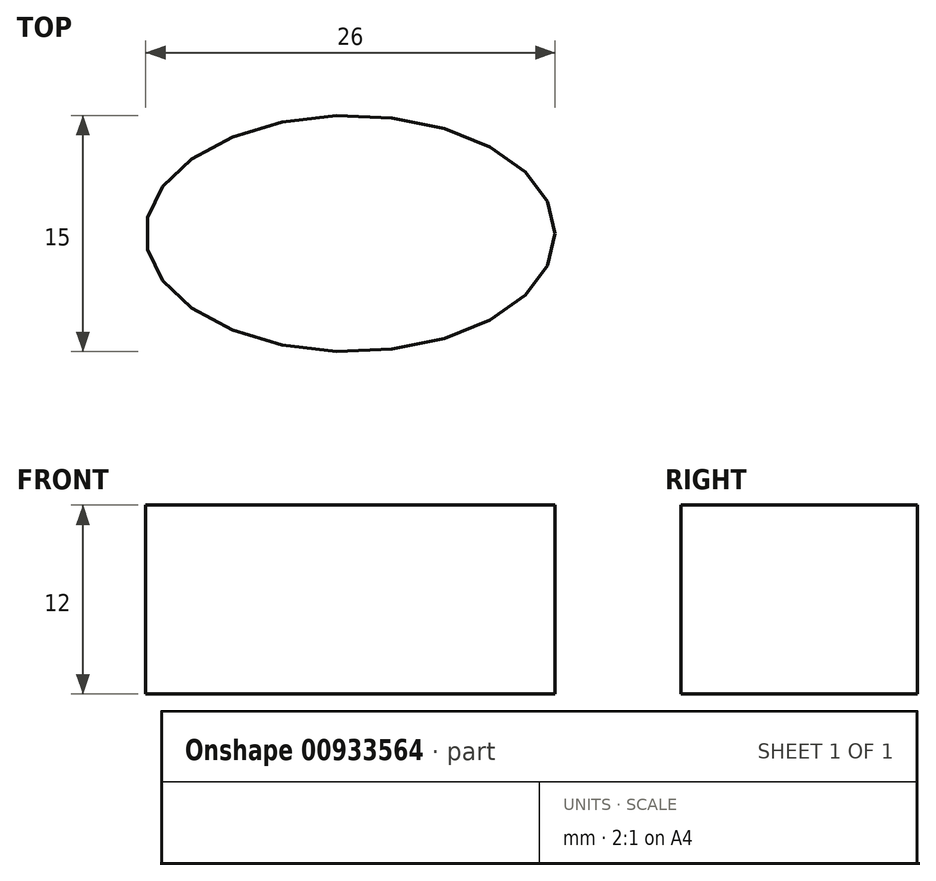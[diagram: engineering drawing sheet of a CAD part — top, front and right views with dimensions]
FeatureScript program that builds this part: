
annotation { "Feature Type Name" : "Feature", "Feature Type Description" : "" }
export const myFeature = defineFeature(function(context is Context, id is Id, definition is map)
    precondition{}
    {
        {
            var Q0;
            Q0=qCreatedBy(makeId("Top.planeOp"),FACE);
            var sketch = newSketch(context, id + "F0", { "sketchPlane" : qUnion([Q0])});
            skEllipse(sketch, "E0", {"center": v(0, 0) * mm, "majorRadius": 13 * mm, "minorRadius": 7.5 * mm, "majorAxis": v(1, 0)});
            skSolve(sketch);
        }
        {
            var Q0;
            Q0 = qSketchRegion(id + "F0", true);
            extrude(context, id + "F1", {"entities" : qUnion([Q0]), "oppositeDirection" : true, "depth" : 12 * mm, "offsetDistance" : 25 * mm});
        }
    });
